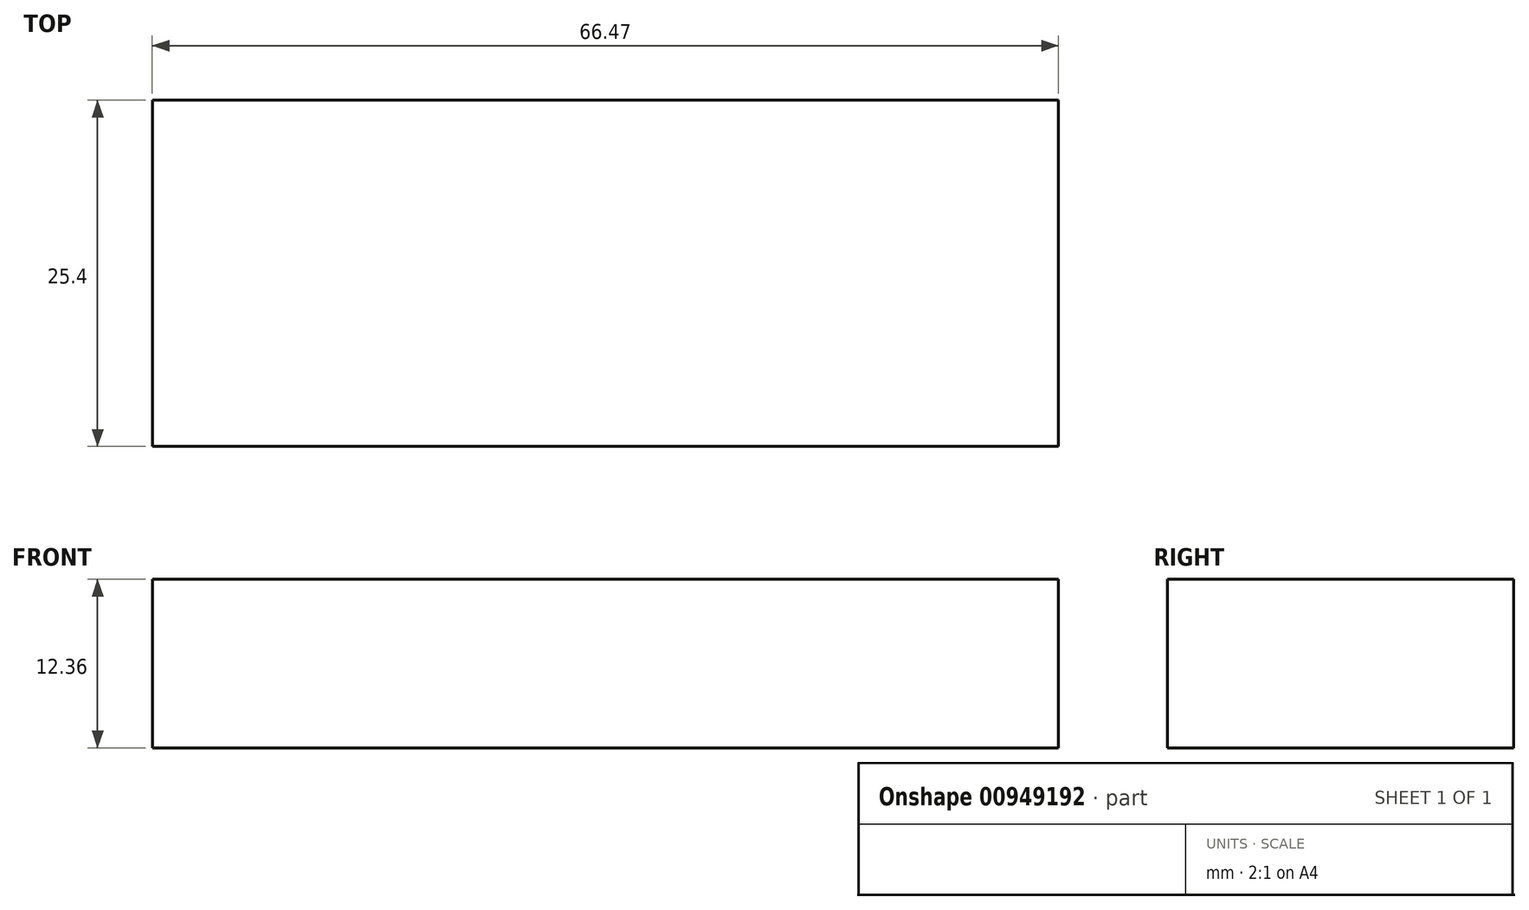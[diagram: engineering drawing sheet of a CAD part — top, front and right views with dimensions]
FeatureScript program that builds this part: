
annotation { "Feature Type Name" : "Feature", "Feature Type Description" : "" }
export const myFeature = defineFeature(function(context is Context, id is Id, definition is map)
    precondition{}
    {
        {
            var Q0;
            Q0=qCreatedBy(makeId("Front.planeOp"),FACE);
            var sketch = newSketch(context, id + "F0", { "sketchPlane" : qUnion([Q0])});
            skLineSegment(sketch, "E0", {"start": v(-32.2, 12.36) * mm, "end": v(34.26, 12.36) * mm});
            skLineSegment(sketch, "E1", {"start": v(34.26, 12.36) * mm, "end": v(34.26, 0) * mm});
            skLineSegment(sketch, "E2", {"start": v(34.26, 0) * mm, "end": v(-32.2, 0) * mm});
            skLineSegment(sketch, "E3", {"start": v(-32.2, 0) * mm, "end": v(-32.2, 12.36) * mm});
            skSolve(sketch);
        }
        {
            var Q0;
            Q0 = qSketchRegion(id + "F0", true);
            extrude(context, id + "F1", {"entities" : qUnion([Q0]), "depth" : 25.4 * mm, "offsetDistance" : 25.4 * mm});
        }
    });
